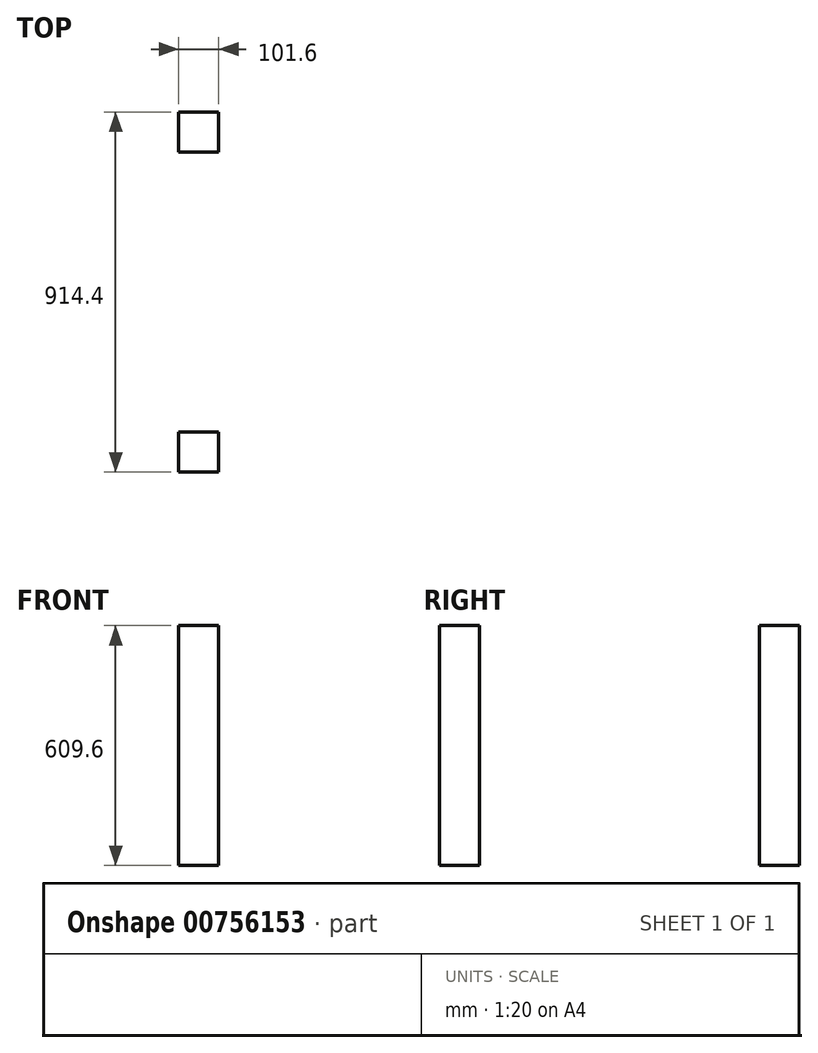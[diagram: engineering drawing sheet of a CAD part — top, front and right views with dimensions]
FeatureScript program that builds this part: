
annotation { "Feature Type Name" : "Feature", "Feature Type Description" : "" }
export const myFeature = defineFeature(function(context is Context, id is Id, definition is map)
    precondition{}
    {
        {
            var Q0;
            Q0=qCreatedBy(makeId("Top.planeOp"),FACE);
            var sketch = newSketch(context, id + "F0", { "sketchPlane" : qUnion([Q0])});
            skLineSegment(sketch, "E0.bottom", {"start": v(-914.4, 457.2) * mm, "end": v(914.4, 457.2) * mm, "construction": true});
            skLineSegment(sketch, "E0.top", {"start": v(-914.4, -457.2) * mm, "end": v(914.4, -457.2) * mm, "construction": true});
            skLineSegment(sketch, "E0.left", {"start": v(-914.4, 457.2) * mm, "end": v(-914.4, -457.2) * mm, "construction": true});
            skLineSegment(sketch, "E0.right", {"start": v(914.4, 457.2) * mm, "end": v(914.4, -457.2) * mm, "construction": true});
            skLineSegment(sketch, "E1", {"start": v(-914.4, 457.2) * mm, "end": v(914.4, -457.2) * mm, "construction": true});
            skSolve(sketch);
        }
        {
            var Q0;
            Q0=qCreatedBy(makeId("Top.planeOp"),FACE);
            var sketch = newSketch(context, id + "F1", { "sketchPlane" : qUnion([Q0])});
            skLineSegment(sketch, "E2.bottom", {"start": v(914.4, 457.2) * mm, "end": v(812.8, 457.2) * mm});
            skLineSegment(sketch, "E2.top", {"start": v(914.4, 355.6) * mm, "end": v(812.8, 355.6) * mm});
            skLineSegment(sketch, "E2.left", {"start": v(914.4, 457.2) * mm, "end": v(914.4, 355.6) * mm});
            skLineSegment(sketch, "E2.right", {"start": v(812.8, 457.2) * mm, "end": v(812.8, 355.6) * mm});
            skLineSegment(sketch, "E3.bottom", {"start": v(812.8, -355.6) * mm, "end": v(914.4, -355.6) * mm});
            skLineSegment(sketch, "E3.top", {"start": v(812.8, -457.2) * mm, "end": v(914.4, -457.2) * mm});
            skLineSegment(sketch, "E3.left", {"start": v(812.8, -355.6) * mm, "end": v(812.8, -457.2) * mm});
            skLineSegment(sketch, "E3.right", {"start": v(914.4, -355.6) * mm, "end": v(914.4, -457.2) * mm});
            skSolve(sketch);
        }
        {
            var Q0;
            Q0=makeQuery(id+"F1.imprint","IMPRINT",FACE,{"disambiguationData":[TD([[makeQuery(id+"F1.imprint","IMPRINT",EDGE,{"derivedFrom":sQuery(id+"F1.wireOp",EDGE,"E3.bottom")}),-1.0]])]});
            var Q1;
            Q1=makeQuery(id+"F1.imprint","IMPRINT",FACE,{"disambiguationData":[TD([[makeQuery(id+"F1.imprint","IMPRINT",EDGE,{"derivedFrom":sQuery(id+"F1.wireOp",EDGE,"E2.bottom")}),1.0]])]});
            extrude(context, id + "F2", {"entities" : qUnion([Q0, Q1]), "oppositeDirection" : true, "depth" : 609.6 * mm, "offsetDistance" : 30.48 * mm});
        }
    });
